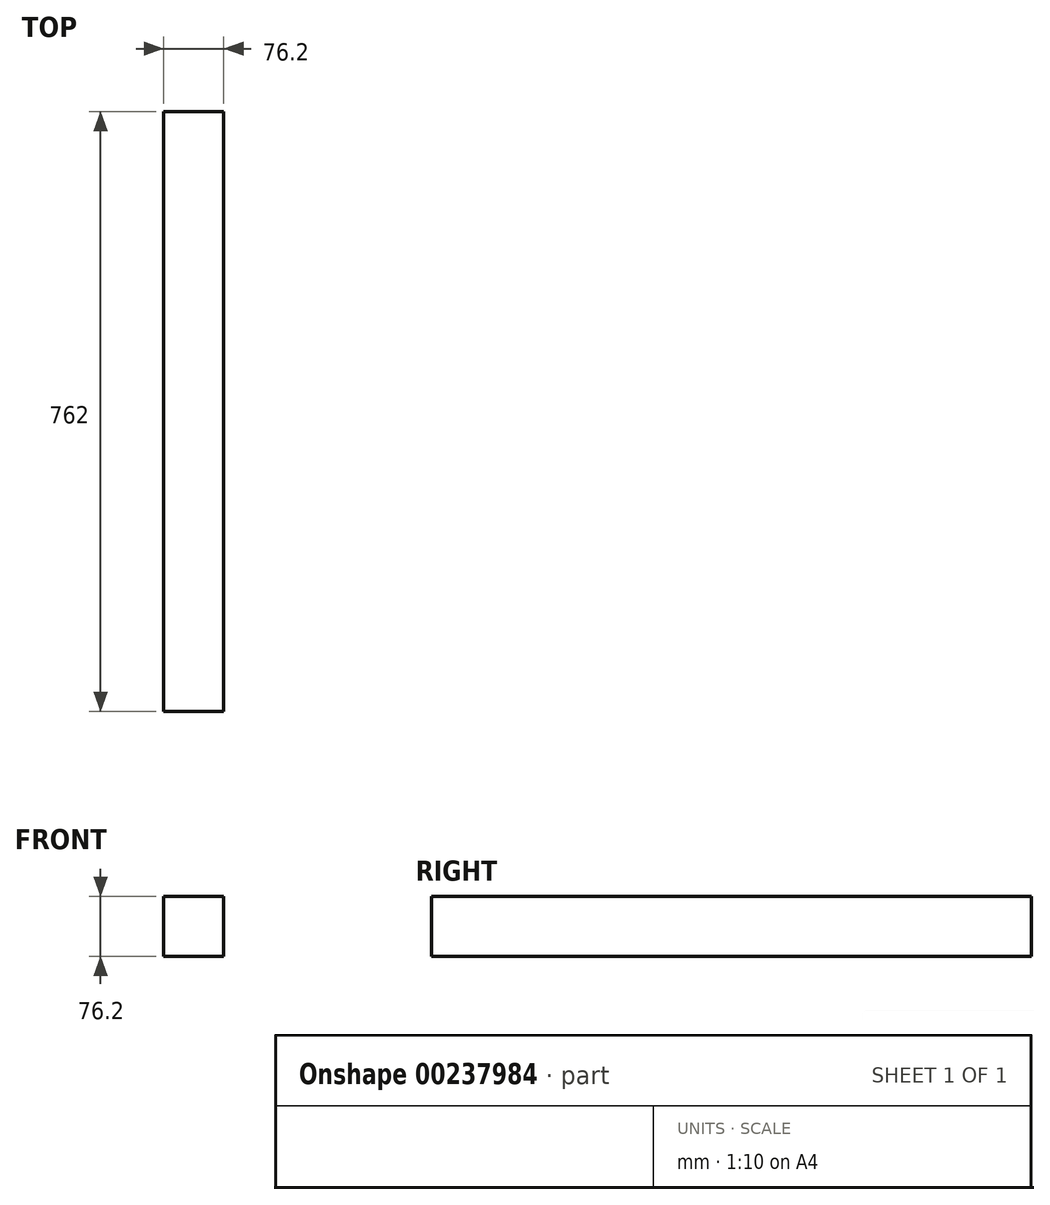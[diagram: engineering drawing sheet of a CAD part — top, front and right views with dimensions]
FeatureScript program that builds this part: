
annotation { "Feature Type Name" : "Feature", "Feature Type Description" : "" }
export const myFeature = defineFeature(function(context is Context, id is Id, definition is map)
    precondition{}
    {
        {
            var Q0;
            Q0=qCreatedBy(makeId("Front.planeOp"),FACE);
            var sketch = newSketch(context, id + "F0", { "sketchPlane" : qUnion([Q0])});
            skLineSegment(sketch, "E0.bottom", {"start": v(38.1, -38.1) * mm, "end": v(-38.1, -38.1) * mm});
            skLineSegment(sketch, "E0.top", {"start": v(38.1, 38.1) * mm, "end": v(-38.1, 38.1) * mm});
            skLineSegment(sketch, "E0.left", {"start": v(38.1, -38.1) * mm, "end": v(38.1, 38.1) * mm});
            skLineSegment(sketch, "E0.right", {"start": v(-38.1, -38.1) * mm, "end": v(-38.1, 38.1) * mm});
            skPoint(sketch, "E0.middle", {"position": v(0, 0) * mm});
            skSolve(sketch);
        }
        {
            var Q0;
            Q0 = qSketchRegion(id + "F0", true);
            extrude(context, id + "F1", {"entities" : qUnion([Q0]), "depth" : 762 * mm, "symmetric" : true});
        }
    });
